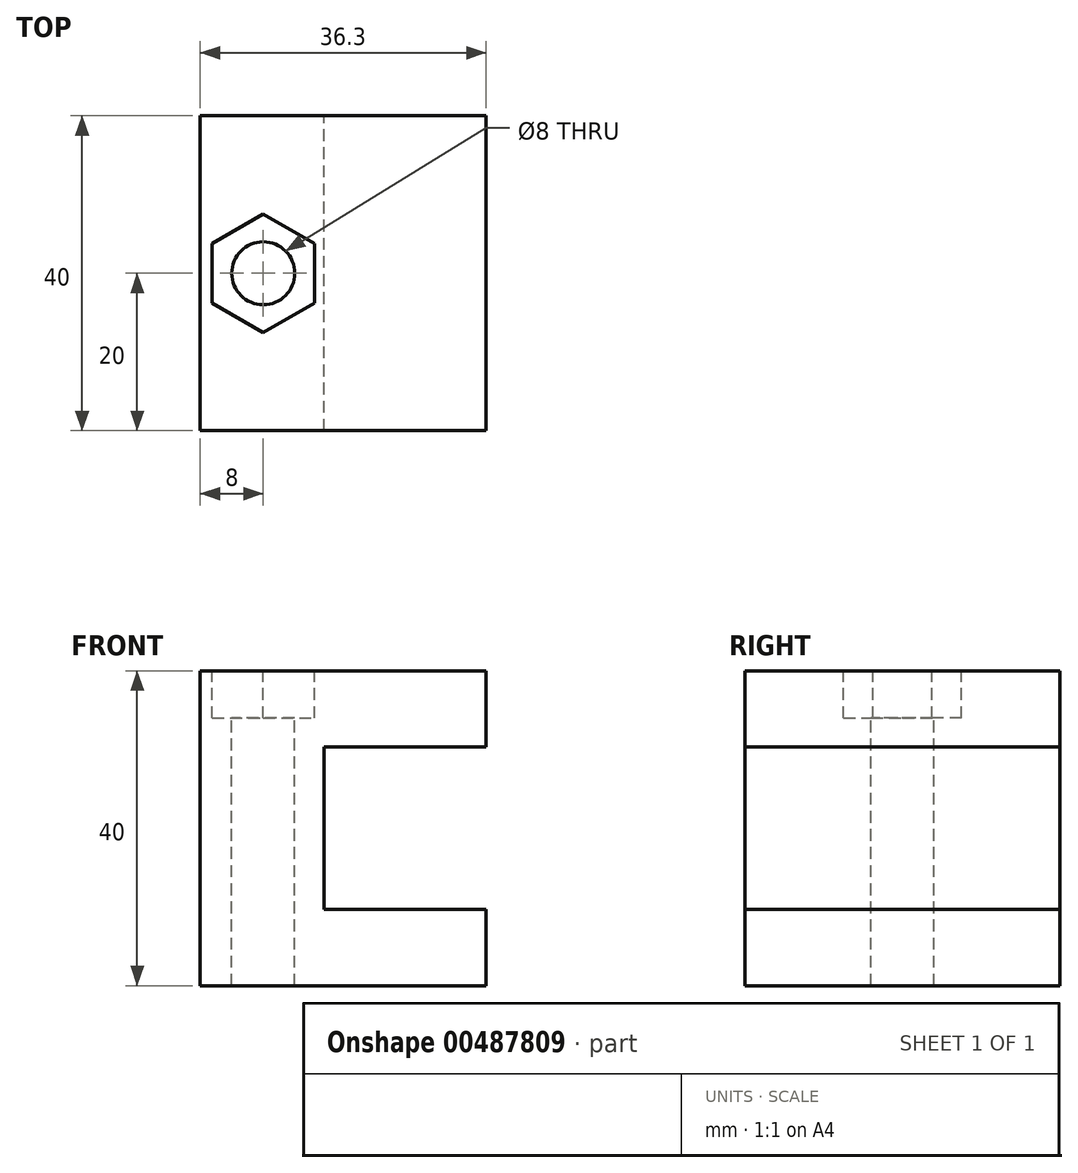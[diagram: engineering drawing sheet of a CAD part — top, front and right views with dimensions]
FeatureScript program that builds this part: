
annotation { "Feature Type Name" : "Feature", "Feature Type Description" : "" }
export const myFeature = defineFeature(function(context is Context, id is Id, definition is map)
    precondition{}
    {
        {
            var Q0;
            Q0=qCreatedBy(makeId("Front.planeOp"),FACE);
            var sketch = newSketch(context, id + "F0", { "sketchPlane" : qUnion([Q0])});
            skLineSegment(sketch, "E0.bottom", {"start": v(10.3, -10.3) * mm, "end": v(-10.3, -10.3) * mm});
            skLineSegment(sketch, "E0.top", {"start": v(10.3, 10.3) * mm, "end": v(-10.3, 10.3) * mm});
            skLineSegment(sketch, "E0.left", {"start": v(10.3, -10.3) * mm, "end": v(10.3, 10.3) * mm});
            skLineSegment(sketch, "E0.right", {"start": v(-10.3, -10.3) * mm, "end": v(-10.3, 10.3) * mm});
            skPoint(sketch, "E0.middle", {"position": v(0, 0) * mm});
            skLineSegment(sketch, "E1.bottom", {"start": v(2.4, -10.3) * mm, "end": v(-2.4, -10.3) * mm});
            skLineSegment(sketch, "E1.top", {"start": v(2.4, 10.3) * mm, "end": v(-2.4, 10.3) * mm});
            skLineSegment(sketch, "E1.left", {"start": v(2.4, -10.3) * mm, "end": v(2.4, 10.3) * mm});
            skLineSegment(sketch, "E1.right", {"start": v(-2.4, -10.3) * mm, "end": v(-2.4, 10.3) * mm});
            skLineSegment(sketch, "E2.bottom", {"start": v(2.4, -8.3) * mm, "end": v(-2.4, -8.3) * mm});
            skLineSegment(sketch, "E2.top", {"start": v(2.4, 8.3) * mm, "end": v(-2.4, 8.3) * mm});
            skLineSegment(sketch, "E2.left", {"start": v(2.4, -8.3) * mm, "end": v(2.4, 8.3) * mm});
            skLineSegment(sketch, "E2.right", {"start": v(-2.4, -8.3) * mm, "end": v(-2.4, 8.3) * mm});
            skLineSegment(sketch, "E3.bottom", {"start": v(26, -20) * mm, "end": v(-26, -20) * mm});
            skLineSegment(sketch, "E3.top", {"start": v(26, 20) * mm, "end": v(-26, 20) * mm});
            skLineSegment(sketch, "E3.left", {"start": v(26, -20) * mm, "end": v(26, 20) * mm});
            skLineSegment(sketch, "E3.right", {"start": v(-26, -20) * mm, "end": v(-26, 20) * mm});
            skLineSegment(sketch, "E4", {"start": v(10.3, 20) * mm, "end": v(10.3, 10.3) * mm});
            skLineSegment(sketch, "E5", {"start": v(10.3, -10.3) * mm, "end": v(10.3, -20) * mm});
            skLineSegment(sketch, "E6.bottom", {"start": v(-10.3, 2.4) * mm, "end": v(10.3, 2.4) * mm});
            skLineSegment(sketch, "E6.top", {"start": v(-10.3, -2.4) * mm, "end": v(10.3, -2.4) * mm});
            skLineSegment(sketch, "E6.left", {"start": v(-10.3, 2.4) * mm, "end": v(-10.3, -2.4) * mm});
            skLineSegment(sketch, "E6.right", {"start": v(10.3, 2.4) * mm, "end": v(10.3, -2.4) * mm});
            skLineSegment(sketch, "E7.bottom", {"start": v(8.3, -2.4) * mm, "end": v(-8.3, -2.4) * mm});
            skLineSegment(sketch, "E7.top", {"start": v(8.3, 2.4) * mm, "end": v(-8.3, 2.4) * mm});
            skLineSegment(sketch, "E7.left", {"start": v(8.3, -2.4) * mm, "end": v(8.3, 2.4) * mm});
            skLineSegment(sketch, "E7.right", {"start": v(-8.3, -2.4) * mm, "end": v(-8.3, 2.4) * mm});
            skSolve(sketch);
        }
        {
            var Q0;
            {var subQ0=sQuery(id+"F0.wireOp",EDGE,"E0.right");Q0=makeQuery(id+"F0.imprint","IMPRINT",FACE,{"disambiguationData":[TD([[makeQuery(id+"F0.imprint","IMPRINT",EDGE,{"derivedFrom":subQ0}),1.0]])]});}
            var Q1;
            {var subQ0=sQuery(id+"F0.wireOp",EDGE,"E1.bottom");Q1=makeQuery(id+"F0.imprint","IMPRINT",FACE,{"disambiguationData":[TD([[makeQuery(id+"F0.imprint","IMPRINT",EDGE,{"derivedFrom":subQ0}),-1.0]])]});}
            var Q2;
            {var subQ0=sQuery(id+"F0.wireOp",EDGE,"E1.top");Q2=makeQuery(id+"F0.imprint","IMPRINT",FACE,{"disambiguationData":[TD([[makeQuery(id+"F0.imprint","IMPRINT",EDGE,{"derivedFrom":subQ0}),1.0]])]});}
            var Q3;
            {var subQ0=sQuery(id+"F0.wireOp",EDGE,"E6.left");Q3=makeQuery(id+"F0.imprint","IMPRINT",FACE,{"disambiguationData":[TD([[makeQuery(id+"F0.imprint","IMPRINT",EDGE,{"derivedFrom":subQ0}),1.0]])]});}
            extrude(context, id + "F1", {"entities" : qUnion([Q0, Q1, Q2, Q3]), "endBound" : BoundingType.SYMMETRIC, "depth" : 40 * mm, "offsetDistance" : 25 * mm});
        }
        {
            var Q0;
            Q0=makeQuery(id+"F1.opExtrude","SWEPT_FACE",FACE,{"disambiguationData":[OSD([sQuery(id+"F0.wireOp",EDGE,"E3.top")])]});
            var sketch = newSketch(context, id + "F2", { "sketchPlane" : qUnion([Q0])});
            skCircle(sketch, "E8", {"center": v(-18, 0) * mm, "radius": 4 * mm});
            skCircle(sketch, "E9.cCircle", {"center": v(-18, 0) * mm, "radius": 6.5 * mm, "construction": true});
            skLineSegment(sketch, "E9.0", {"start": v(-11.5, 3.75) * mm, "end": v(-11.5, -3.75) * mm});
            skLineSegment(sketch, "E9.1", {"start": v(-11.5, -3.75) * mm, "end": v(-18, -7.5) * mm});
            skLineSegment(sketch, "E9.2", {"start": v(-18, -7.5) * mm, "end": v(-24.5, -3.75) * mm});
            skLineSegment(sketch, "E9.3", {"start": v(-24.5, -3.75) * mm, "end": v(-24.5, 3.75) * mm});
            skLineSegment(sketch, "E9.4", {"start": v(-24.5, 3.75) * mm, "end": v(-18, 7.5) * mm});
            skLineSegment(sketch, "E9.5", {"start": v(-18, 7.5) * mm, "end": v(-11.5, 3.75) * mm});
            skPoint(sketch, "E9.0.midPoint", {"position": v(-11.5, 0) * mm});
            skSolve(sketch);
        }
        {
            var Q0;
            Q0=makeQuery(id+"F2.imprint","IMPRINT",FACE,{"disambiguationData":[TD([[makeQuery(id+"F2.imprint","IMPRINT",EDGE,{"derivedFrom":sQuery(id+"F2.wireOp",EDGE,"E8")}),1.0]])]});
            extrude(context, id + "F3", {"entities" : qUnion([Q0]), "operationType" : NewBodyOperationType.REMOVE, "oppositeDirection" : true, "depth" : 50 * mm, "offsetDistance" : 25 * mm});
        }
        {
            var Q0;
            Q0=makeQuery(id+"F2.imprint","IMPRINT",FACE,{"disambiguationData":[TD([[makeQuery(id+"F2.imprint","IMPRINT",EDGE,{"derivedFrom":sQuery(id+"F2.wireOp",EDGE,"E8")}),-1.0]])]});
            extrude(context, id + "F4", {"entities" : qUnion([Q0]), "operationType" : NewBodyOperationType.REMOVE, "oppositeDirection" : true, "depth" : 6 * mm, "offsetDistance" : 25 * mm});
        }
    });
